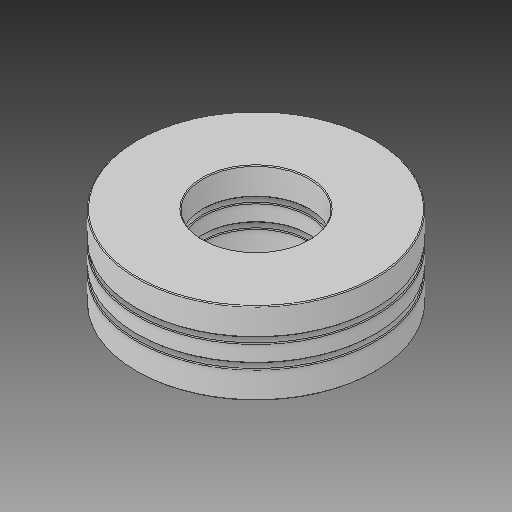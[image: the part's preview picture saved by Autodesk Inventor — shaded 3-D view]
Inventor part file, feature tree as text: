
AUTODESK INVENTOR PART (.ipt)
format: ipt  version: 2019 (Build 230136000, 136)  size: 507,904 bytes
history: native  units: in
note: dims shown in document units (in); Inventor stores cm internally (conversion verified against a paired STEP export)
features: other x6, fillet x3, revolve x1
ambient origin geometry x8: Origin, YZ Plane, XZ Plane, XY Plane, X Axis, Y Axis, Z Axis, Center Point
bodies: Solid1 (feature_tree), Solid2 (feature_tree), Solid3 (feature_tree), Solid4 (feature_tree), Solid5 (feature_tree), Solid6 (feature_tree), Solid7 (feature_tree), Solid8 (feature_tree), Solid9 (feature_tree), Solid10 (feature_tree)
feature tree (10):
  revolve  "Revolve2"  [1 undecoded]
  other  "CirPattern1[1]"
  other  "CirPattern1[2]"
  other  "CirPattern1[3]"
  other  "CirPattern1[4]"
  other  "CirPattern1[5]"
  other  "CirPattern1[6]"
  fillet  "Fillet2"  [1 undecoded]
  fillet  "Fillet1"  [1 undecoded]
  fillet  "Fillet3"  [1 undecoded]
note: 4 required parameter values undecoded (feature->parameter linkage not recoverable at this tier; creation-order binding heuristic only, values carry confidence <= 0.55)
